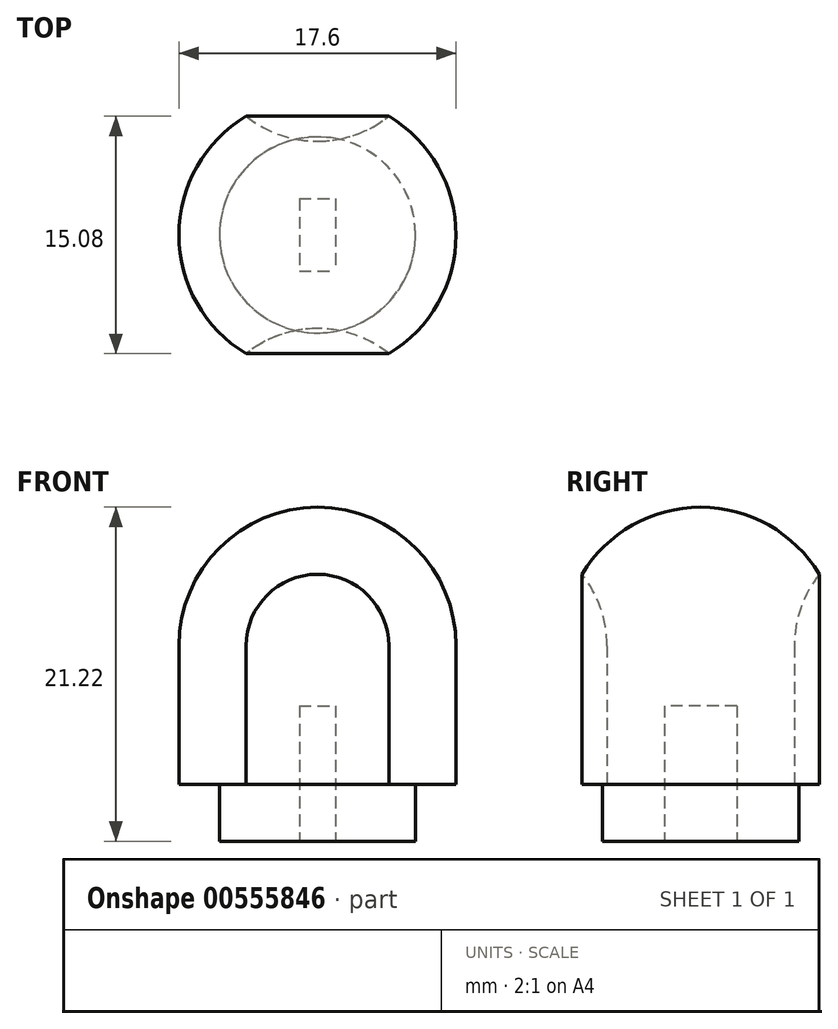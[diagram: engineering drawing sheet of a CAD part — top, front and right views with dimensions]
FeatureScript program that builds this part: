
annotation { "Feature Type Name" : "Feature", "Feature Type Description" : "" }
export const myFeature = defineFeature(function(context is Context, id is Id, definition is map)
    precondition{}
    {
        {
            var Q0;
            Q0=qCreatedBy(makeId("Top.planeOp"),FACE);
            var sketch = newSketch(context, id + "F0", { "sketchPlane" : qUnion([Q0])});
            skCircle(sketch, "E0", {"center": v(-54.58, 22.06) * mm, "radius": 6.23 * mm});
            skCircle(sketch, "E1", {"center": v(-54.58, 22.06) * mm, "radius": 8.8 * mm});
            skCircle(sketch, "E2", {"center": v(-54.58, 35.26) * mm, "radius": 7.25 * mm});
            skCircle(sketch, "E3", {"center": v(-54.58, 8.86) * mm, "radius": 7.25 * mm});
            skSolve(sketch);
        }
        {
            var Q0;
            {var subQ0=sQuery(id+"F0.wireOp",EDGE,"E2");var subQ1=sQuery(id+"F0.wireOp",EDGE,"E0");var subQ2=makeQuery(id+"F0.imprint","INTERSECT",VERTEX,{"disambiguationData":[OD(0.0)],"derivedFrom":[subQ1,subQ0]});Q0=makeQuery(id+"F0.imprint","IMPRINT",FACE,{"disambiguationData":[TD([[makeQuery(id+"F0.imprint","IMPRINT",EDGE,{"disambiguationData":[TD([[subQ2,-1.0]])],"derivedFrom":subQ1}),-1.0]])]});}
            var Q1;
            {var subQ0=sQuery(id+"F0.wireOp",EDGE,"E2");var subQ1=sQuery(id+"F0.wireOp",EDGE,"E0");var subQ2=makeQuery(id+"F0.imprint","INTERSECT",VERTEX,{"disambiguationData":[OD(1.0)],"derivedFrom":[subQ1,subQ0]});Q1=makeQuery(id+"F0.imprint","IMPRINT",FACE,{"disambiguationData":[TD([[makeQuery(id+"F0.imprint","IMPRINT",EDGE,{"disambiguationData":[TD([[subQ2,1.0]])],"derivedFrom":subQ1}),-1.0]])]});}
            var Q2;
            {var subQ0=sQuery(id+"F0.wireOp",EDGE,"E2");var subQ1=sQuery(id+"F0.wireOp",EDGE,"E0");var subQ2=makeQuery(id+"F0.imprint","INTERSECT",VERTEX,{"disambiguationData":[OD(0.0)],"derivedFrom":[subQ1,subQ0]});Q2=makeQuery(id+"F0.imprint","IMPRINT",FACE,{"disambiguationData":[TD([[makeQuery(id+"F0.imprint","IMPRINT",EDGE,{"disambiguationData":[TD([[subQ2,-1.0]])],"derivedFrom":subQ1}),1.0]])]});}
            extrude(context, id + "F1", {"entities" : qUnion([Q0, Q1, Q2]), "depth" : 8.8 * mm, "offsetDistance" : 25 * mm});
        }
        {
            var Q0;
            {var subQ0=sQuery(id+"F0.wireOp",EDGE,"E2");var subQ1=sQuery(id+"F0.wireOp",EDGE,"E0");var subQ2=makeQuery(id+"F0.imprint","INTERSECT",VERTEX,{"disambiguationData":[OD(0.0)],"derivedFrom":[subQ1,subQ0]});Q0=makeQuery(id+"F0.imprint","IMPRINT",FACE,{"disambiguationData":[TD([[makeQuery(id+"F0.imprint","IMPRINT",EDGE,{"disambiguationData":[TD([[subQ2,-1.0]])],"derivedFrom":subQ1}),1.0]])]});}
            var Q1;
            {var subQ0=sQuery(id+"F0.wireOp",EDGE,"E3");var subQ1=sQuery(id+"F0.wireOp",EDGE,"E0");var subQ2=makeQuery(id+"F0.imprint","INTERSECT",VERTEX,{"disambiguationData":[OD(0.0)],"derivedFrom":[subQ1,subQ0]});Q1=makeQuery(id+"F0.imprint","IMPRINT",FACE,{"disambiguationData":[TD([[makeQuery(id+"F0.imprint","IMPRINT",EDGE,{"disambiguationData":[TD([[subQ2,-1.0]])],"derivedFrom":subQ1}),1.0]])]});}
            var Q2;
            {var subQ0=sQuery(id+"F0.wireOp",EDGE,"E2");var subQ1=sQuery(id+"F0.wireOp",EDGE,"E0");var subQ2=makeQuery(id+"F0.imprint","INTERSECT",VERTEX,{"disambiguationData":[OD(0.0)],"derivedFrom":[subQ1,subQ0]});Q2=makeQuery(id+"F0.imprint","IMPRINT",FACE,{"disambiguationData":[TD([[makeQuery(id+"F0.imprint","IMPRINT",EDGE,{"disambiguationData":[TD([[subQ2,1.0]])],"derivedFrom":subQ1}),1.0]])]});}
            extrude(context, id + "F2", {"entities" : qUnion([Q0, Q1, Q2]), "operationType" : NewBodyOperationType.ADD, "oppositeDirection" : true, "depth" : 3.62 * mm, "offsetDistance" : 25 * mm});
        }
        {
            var Q0;
            Q0=makeQuery(id+"F2.opExtrude","CAP_FACE",FACE,{"disambiguationData":[OSD([sQuery(id+"F0.wireOp",EDGE,"E0")])],"isStart":false});
            var sketch = newSketch(context, id + "F3", { "sketchPlane" : qUnion([Q0])});
            skLineSegment(sketch, "E4.bottom", {"start": v(-54.58, -22.06) * mm, "end": v(-53.43, -22.06) * mm});
            skLineSegment(sketch, "E4.top", {"start": v(-54.58, -19.76) * mm, "end": v(-53.43, -19.76) * mm});
            skLineSegment(sketch, "E4.left", {"start": v(-54.58, -22.06) * mm, "end": v(-54.58, -19.76) * mm});
            skLineSegment(sketch, "E4.right", {"start": v(-53.43, -22.06) * mm, "end": v(-53.43, -19.76) * mm});
            skLineSegment(sketch, "E5.top", {"start": v(-54.58, -24.36) * mm, "end": v(-53.43, -24.36) * mm});
            skLineSegment(sketch, "E5.left", {"start": v(-54.58, -22.06) * mm, "end": v(-54.58, -24.36) * mm});
            skLineSegment(sketch, "E5.right", {"start": v(-53.43, -22.06) * mm, "end": v(-53.43, -24.36) * mm});
            skLineSegment(sketch, "E6.bottom", {"start": v(-54.58, -22.06) * mm, "end": v(-55.73, -22.06) * mm});
            skLineSegment(sketch, "E6.top", {"start": v(-54.58, -24.36) * mm, "end": v(-55.73, -24.36) * mm});
            skLineSegment(sketch, "E6.right", {"start": v(-55.73, -22.06) * mm, "end": v(-55.73, -24.36) * mm});
            skLineSegment(sketch, "E7.top", {"start": v(-54.58, -19.76) * mm, "end": v(-55.73, -19.76) * mm});
            skLineSegment(sketch, "E7.right", {"start": v(-55.73, -22.06) * mm, "end": v(-55.73, -19.76) * mm});
            skSolve(sketch);
        }
        {
            var Q0;
            Q0 = qSketchRegion(id + "F3", true);
            extrude(context, id + "F4", {"entities" : qUnion([Q0]), "operationType" : NewBodyOperationType.REMOVE, "oppositeDirection" : true, "depth" : 8.6 * mm, "offsetDistance" : 25 * mm});
        }
        {
            var Q0;
            Q0=makeQuery(id+"F1.opExtrude","CAP_FACE",FACE,{"disambiguationData":[OSD([sQuery(id+"F0.wireOp",EDGE,"E1"),sQuery(id+"F0.wireOp",EDGE,"E2"),sQuery(id+"F0.wireOp",EDGE,"E3")])],"isStart":false});
            var sketch = newSketch(context, id + "F5", { "sketchPlane" : qUnion([Q0])});
            skLineSegment(sketch, "E8", {"start": v(-54.58, 22.06) * mm, "end": v(-54.58, 28.01) * mm});
            skLineSegment(sketch, "E9", {"start": v(-54.58, 28.01) * mm, "end": v(-54.58, 16.11) * mm});
            skSolve(sketch);
        }
        {
            var Q0;
            {var subQ0=sQuery(id+"F0.wireOp",EDGE,"E2");var subQ2=sQuery(id+"F0.wireOp",EDGE,"E1");var subQ4=makeQuery(id+"F1.opExtrude","CAP_EDGE",EDGE,{"disambiguationData":[OSD([subQ2]),TDD([makeQuery(id+"F0.imprint","IMPRINT",EDGE,{"disambiguationData":[TD([[makeQuery(id+"F0.imprint","INTERSECT",VERTEX,{"disambiguationData":[OD(0.0)],"derivedFrom":[subQ2,subQ0]}),-1.0]])],"derivedFrom":subQ2})])],"isStart":false});Q0=makeQuery(id+"F5.imprint","IMPRINT",FACE,{"disambiguationData":[TD([[makeQuery(id+"F5.imprint","IMPRINT",EDGE,{"derivedFrom":subQ4}),1.0]])]});}
            var Q1;
            Q1=sQuery(id+"F5.wireOp",EDGE,"E9");
            revolve(context, id + "F6", {"operationType" : NewBodyOperationType.ADD, "entities" : qUnion([Q0]), "axis" : qUnion([Q1]), "revolveType" : RevolveType.ONE_DIRECTION, "oppositeDirection" : true, "angle" : 180 * degree});
        }
    });
